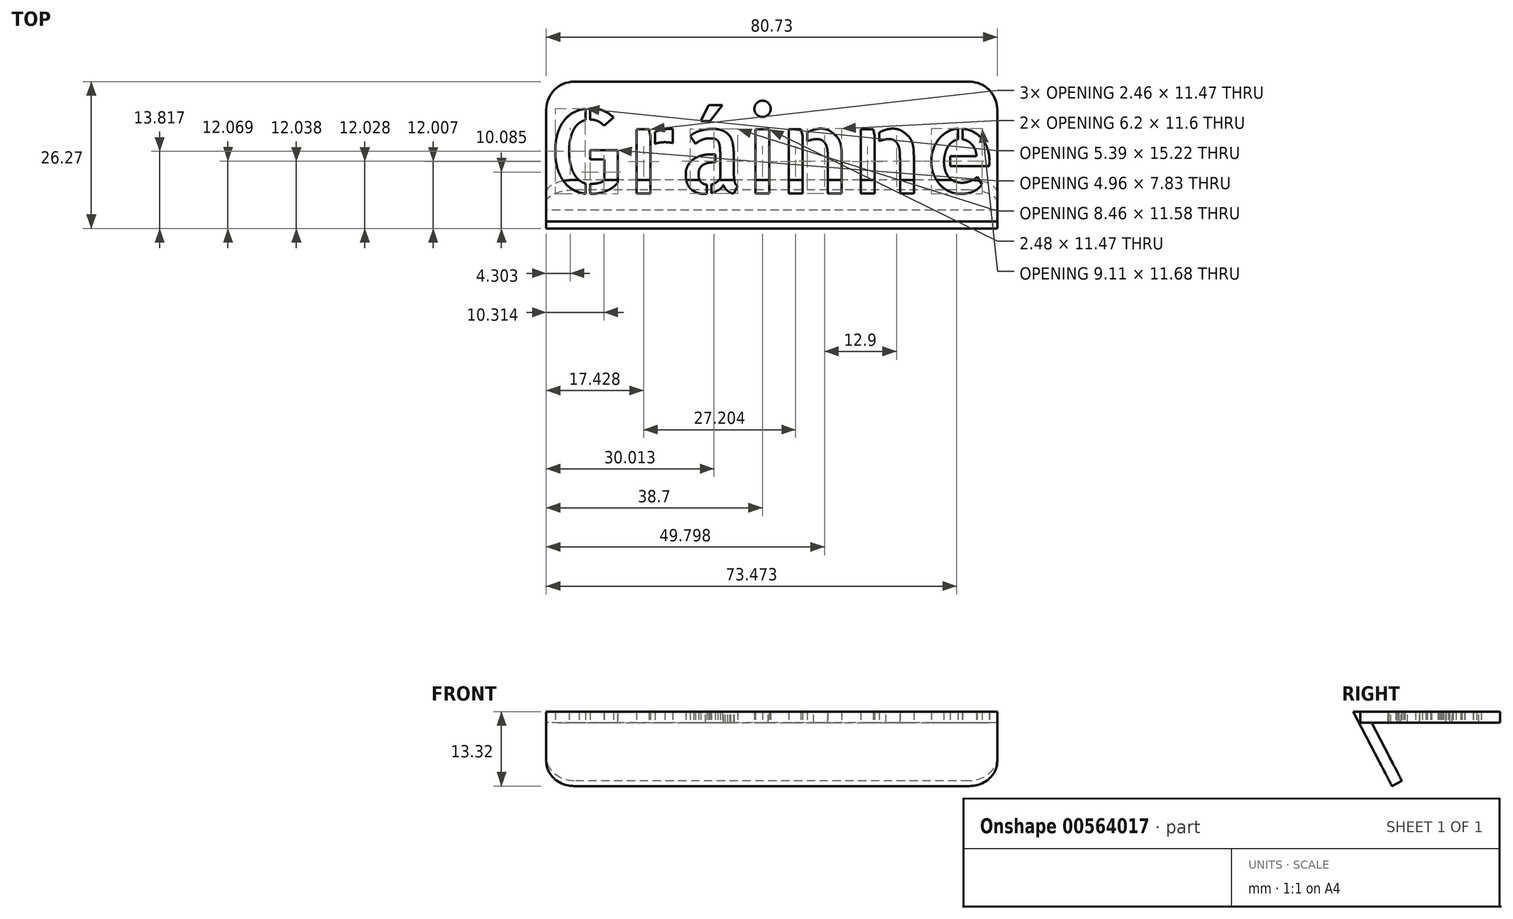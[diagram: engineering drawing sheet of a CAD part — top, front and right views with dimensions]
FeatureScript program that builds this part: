
annotation { "Feature Type Name" : "Feature", "Feature Type Description" : "" }
export const myFeature = defineFeature(function(context is Context, id is Id, definition is map)
    precondition{}
    {
        {
            var Q0;
            Q0=qCreatedBy(makeId("Top.planeOp"),FACE);
            var sketch = newSketch(context, id + "F0", { "sketchPlane" : qUnion([Q0])});
            skLineSegment(sketch, "E0.bottom", {"start": v(-23.58, 12.5) * mm, "end": v(57.15, 12.5) * mm});
            skLineSegment(sketch, "E0.top", {"start": v(-23.58, -12.5) * mm, "end": v(57.15, -12.5) * mm});
            skLineSegment(sketch, "E0.left", {"start": v(-23.58, 12.5) * mm, "end": v(-23.58, -12.5) * mm});
            skLineSegment(sketch, "E0.right", {"start": v(57.15, 12.5) * mm, "end": v(57.15, -12.5) * mm});
            skText(sketch, "E1", { "text": "Gráinne", "fontName": "AllertaStencil-Regular.ttf"});
            const initialGuessF0  = {"E1": [-0.02358, -0.0075, 1, 0, 0.015]};
            skSetInitialGuess(sketch, initialGuessF0);
            skSolve(sketch);
        }
        {
            var Q0;
            Q0=makeQuery(id+"F0.imprint","IMPRINT",FACE,{"disambiguationData":[TD([[makeQuery(id+"F0.imprint","IMPRINT",EDGE,{"derivedFrom":sQuery(id+"F0.wireOp",EDGE,"E0.bottom")}),-1.0]])]});
            extrude(context, id + "F1", {"entities" : qUnion([Q0]), "depth" : 2 * mm, "offsetDistance" : 25 * mm});
        }
        {
            var Q0;
            {var subQ0=sQuery(id+"F0.wireOp",EDGE,"E0.left");Q0=makeQuery(id+"FYEOEdhl7jzHk82_2.opBoolean","MERGE",FACE,{"derivedFrom":[makeQuery(id+"F1.opExtrude","SWEPT_FACE",FACE,{"disambiguationData":[OSD([subQ0])]}),makeQuery(id+"FOv1BJgTRWeWuMw_1.opExtrude","CAP_FACE",FACE,{"disambiguationData":[OSD([sQuery(id+"F0.wireOp",EDGE,"E0.bottom"),subQ0,sQuery(id+"Fjco5yBOxZZxTCI_1.wireOp",EDGE,"TpTMtmOo-qoIM-rLEy-p7IH-mKgsBanMGF23"),sQuery(id+"Fjco5yBOxZZxTCI_1.wireOp",EDGE,"Ja6BvVoQ-cpFi-Lcom-cL8s-5xC4kZiynyNl"),sQuery(id+"Fjco5yBOxZZxTCI_1.wireOp",EDGE,"utNyaJ8P-FD6r-AD7x-tpFW-fHytfVhziHLl"),sQuery(id+"Fjco5yBOxZZxTCI_1.wireOp",EDGE,"xGzW29bi-H5H8-ObLh-gdKj-mSPkAtMAUUzO")])],"isStart":true})]});}
            var sketch = newSketch(context, id + "F2", { "sketchPlane" : qUnion([Q0])});
            skLineSegment(sketch, "E2", {"start": v(11.52, 2) * mm, "end": v(5.09, -10.4) * mm});
            skLineSegment(sketch, "E3", {"start": v(5.09, -10.4) * mm, "end": v(6.87, -11.32) * mm});
            skLineSegment(sketch, "E4", {"start": v(6.87, -11.32) * mm, "end": v(13.77, 2) * mm});
            skLineSegment(sketch, "E5", {"start": v(13.77, 2) * mm, "end": v(11.52, 2) * mm});
            skSolve(sketch);
        }
        {
            var Q0;
            {var subQ4=sQuery(id+"F2.wireOp",EDGE,"E3");Q0=makeQuery(id+"F2.imprint","IMPRINT",FACE,{"disambiguationData":[TD([[makeQuery(id+"F2.imprint","IMPRINT",EDGE,{"derivedFrom":subQ4}),1.0]])]});}
            var Q1;
            Q1=makeQuery(id+"F1.opExtrude","SWEPT_FACE",FACE,{"disambiguationData":[OSD([sQuery(id+"F0.wireOp",EDGE,"E0.right")])]});
            extrude(context, id + "F3", {"entities" : qUnion([Q0]), "endBound" : BoundingType.UP_TO_SURFACE, "oppositeDirection" : true, "depth" : 75 * mm, "endBoundEntityFace" : qUnion([Q1]), "offsetDistance" : 25 * mm});
        }
        {
            var Q0;
            Q0=makeQuery(id+"F1.opExtrude","SWEPT_EDGE",EDGE,{"disambiguationData":[OSD([sQuery(id+"F0.wireOp",EDGE,"E0.bottom"),sQuery(id+"F0.wireOp",EDGE,"E0.left")])]});
            var Q1;
            Q1=makeQuery(id+"F1.opExtrude","SWEPT_EDGE",EDGE,{"disambiguationData":[OSD([sQuery(id+"F0.wireOp",EDGE,"E0.bottom"),sQuery(id+"F0.wireOp",EDGE,"E0.right")])]});
            var Q2;
            Q2=makeQuery(id+"F3.opExtrude","CAP_EDGE",EDGE,{"disambiguationData":[OSD([sQuery(id+"F2.wireOp",EDGE,"E3")])],"isStart":false});
            var Q3;
            Q3=makeQuery(id+"F3.opExtrude","CAP_EDGE",EDGE,{"disambiguationData":[OSD([sQuery(id+"F2.wireOp",EDGE,"E3")])],"isStart":true});
            var Q4;
            Q4=makeQuery(id+"F3.opExtrude","TWEAK_EDGE",EDGE,{"derivedFrom":[makeQuery(id+"F1.opExtrude","SWEPT_FACE",FACE,{"disambiguationData":[OSD([sQuery(id+"F0.wireOp",EDGE,"E0.right")])]}),makeQuery(id+"F2.imprint","IMPRINT",EDGE,{"derivedFrom":sQuery(id+"F2.wireOp",EDGE,"E3")})]});
            fillet(context, id + "F4", {"entities" : qUnion([Q0, Q1, Q2, Q3, Q4]), "radius" : 5 * mm, "tangentPropagation" : true, "allowEdgeOverflow" : false});
        }
    });
